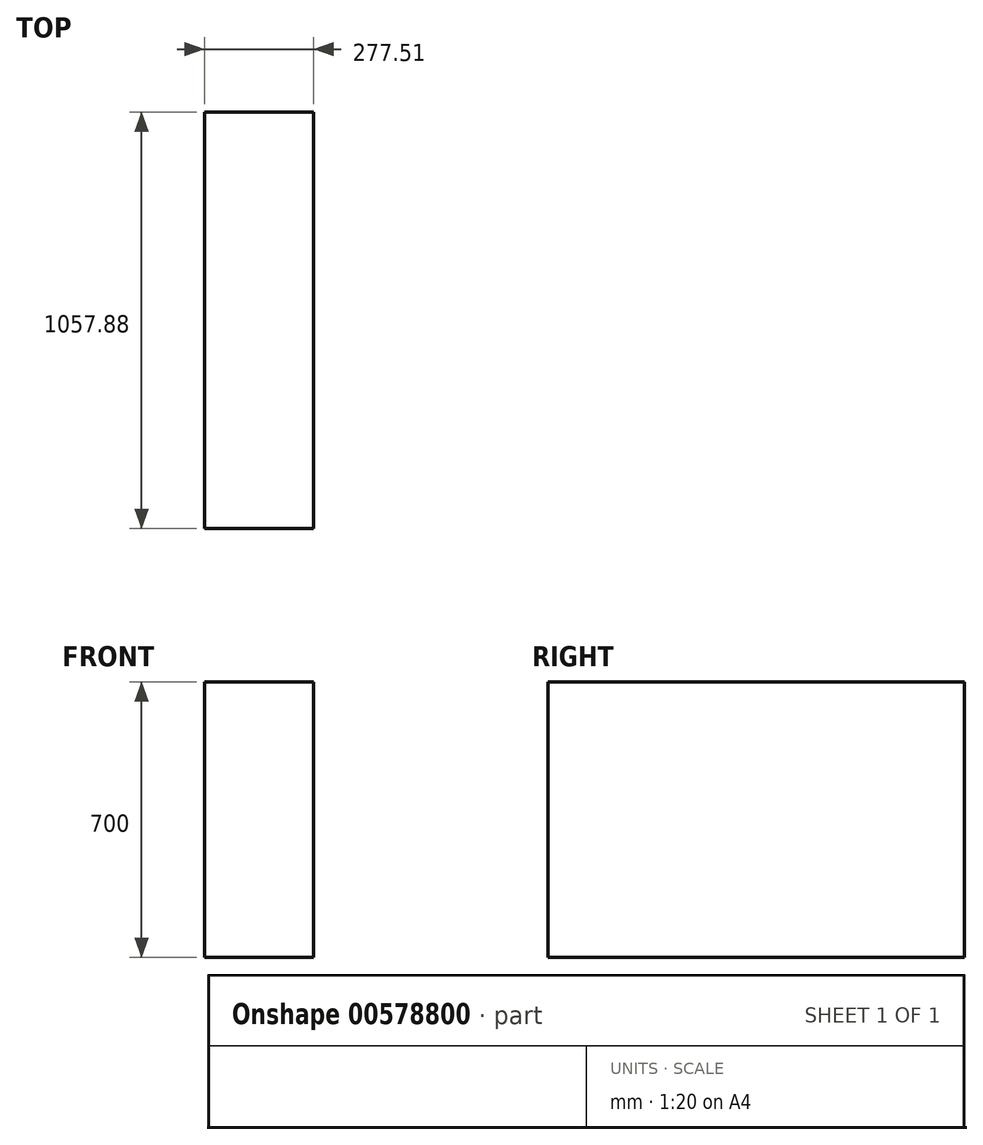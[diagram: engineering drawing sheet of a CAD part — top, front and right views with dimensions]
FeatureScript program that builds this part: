
annotation { "Feature Type Name" : "Feature", "Feature Type Description" : "" }
export const myFeature = defineFeature(function(context is Context, id is Id, definition is map)
    precondition{}
    {
        {
            var Q0;
            Q0=qCreatedBy(makeId("Top.planeOp"),FACE);
            var sketch = newSketch(context, id + "F0", { "sketchPlane" : qUnion([Q0])});
            skLineSegment(sketch, "E0", {"start": v(-48.98, 57.88) * mm, "end": v(53.35, 57.88) * mm});
            skLineSegment(sketch, "E1", {"start": v(53.35, 57.88) * mm, "end": v(53.35, 0) * mm});
            skLineSegment(sketch, "E2", {"start": v(53.35, 0) * mm, "end": v(-48.98, 0) * mm});
            skLineSegment(sketch, "E3", {"start": v(-48.98, 0) * mm, "end": v(-48.98, 57.88) * mm});
            skSolve(sketch);
        }
        {
            var Q0;
            Q0 = qSketchRegion(id + "F0", true);
            extrude(context, id + "F1", {"entities" : qUnion([Q0]), "depth" : 700 * mm, "offsetDistance" : 25 * mm});
        }
        {
            var Q0;
            Q0=makeQuery(id+"F1.opExtrude","SWEPT_FACE",FACE,{"disambiguationData":[OSD([sQuery(id+"F0.wireOp",EDGE,"E2")])]});
            extrude(context, id + "F2", {"entities" : qUnion([Q0]), "operationType" : NewBodyOperationType.ADD, "depth" : 1000 * mm, "offsetDistance" : 25 * mm});
        }
        {
            var Q0;
            {var subQ0=sQuery(id+"F0.wireOp",EDGE,"E1");Q0=makeQuery(id+"F2.boolean.opBoolean","MERGE",FACE,{"derivedFrom":[makeQuery(id+"F1.opExtrude","SWEPT_FACE",FACE,{"disambiguationData":[OSD([subQ0])]}),makeQuery(id+"F2.opExtrude","SWEPT_FACE",FACE,{"disambiguationData":[OSD([subQ0,sQuery(id+"F0.wireOp",EDGE,"E2")])]})]});}
            extrude(context, id + "F3", {"entities" : qUnion([Q0]), "operationType" : NewBodyOperationType.ADD, "depth" : 175.18 * mm, "offsetDistance" : 25 * mm});
        }
    });
